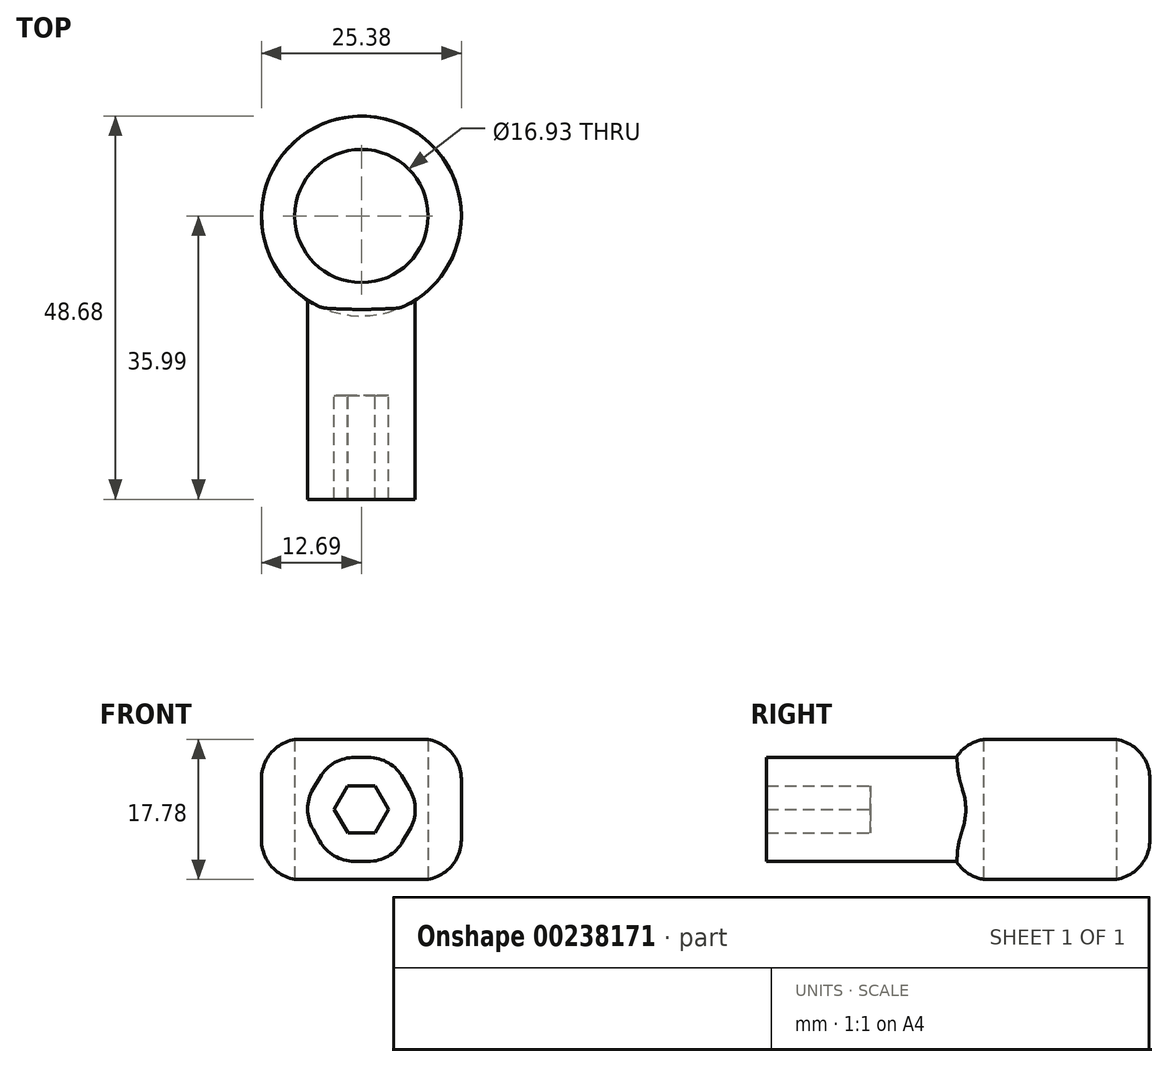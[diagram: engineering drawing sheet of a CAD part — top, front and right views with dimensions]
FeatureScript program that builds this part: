
annotation { "Feature Type Name" : "Feature", "Feature Type Description" : "" }
export const myFeature = defineFeature(function(context is Context, id is Id, definition is map)
    precondition{}
    {
        {
            var Q0;
            Q0=qCreatedBy(makeId("Front.planeOp"),FACE);
            var sketch = newSketch(context, id + "F0", { "sketchPlane" : qUnion([Q0])});
            skCircle(sketch, "E0.cCircle", {"center": v(0, 0) * mm, "radius": 3 * mm, "construction": true});
            skLineSegment(sketch, "E0.0", {"start": v(-1.72, -3) * mm, "end": v(-3.46, -0.01) * mm});
            skLineSegment(sketch, "E0.1", {"start": v(-3.46, -0.01) * mm, "end": v(-1.74, 3) * mm});
            skLineSegment(sketch, "E0.2", {"start": v(-1.74, 3) * mm, "end": v(1.72, 3) * mm});
            skLineSegment(sketch, "E0.3", {"start": v(1.72, 3) * mm, "end": v(3.46, 0.01) * mm});
            skLineSegment(sketch, "E0.4", {"start": v(3.46, 0.01) * mm, "end": v(1.74, -3) * mm});
            skLineSegment(sketch, "E0.5", {"start": v(1.74, -3) * mm, "end": v(-1.72, -3) * mm});
            skPoint(sketch, "E0.0.midPoint", {"position": v(-2.6, -1.51) * mm});
            skCircle(sketch, "E1.cCircle", {"center": v(0, 0) * mm, "radius": 6.6 * mm, "construction": true});
            skLineSegment(sketch, "E1.0", {"start": v(-7.62, 0.04) * mm, "end": v(-3.77, 6.62) * mm});
            skLineSegment(sketch, "E1.1", {"start": v(-3.77, 6.62) * mm, "end": v(3.85, 6.58) * mm});
            skLineSegment(sketch, "E1.2", {"start": v(3.85, 6.58) * mm, "end": v(7.62, -0.04) * mm});
            skLineSegment(sketch, "E1.3", {"start": v(7.62, -0.04) * mm, "end": v(3.77, -6.62) * mm});
            skLineSegment(sketch, "E1.4", {"start": v(3.77, -6.62) * mm, "end": v(-3.85, -6.58) * mm});
            skLineSegment(sketch, "E1.5", {"start": v(-3.85, -6.58) * mm, "end": v(-7.62, 0.04) * mm});
            skPoint(sketch, "E1.0.midPoint", {"position": v(-5.7, 3.33) * mm});
            skSolve(sketch);
        }
        {
            var Q0;
            Q0=makeQuery(id+"F0.imprint","IMPRINT",FACE,{"disambiguationData":[TD([[makeQuery(id+"F0.imprint","IMPRINT",EDGE,{"derivedFrom":sQuery(id+"F0.wireOp",EDGE,"E0.0")}),1.0]])]});
            extrude(context, id + "F1", {"entities" : qUnion([Q0]), "depth" : 25.4 * mm});
        }
        {
            var Q0;
            Q0=makeQuery(id+"F0.imprint","IMPRINT",FACE,{"disambiguationData":[TD([[makeQuery(id+"F0.imprint","IMPRINT",EDGE,{"derivedFrom":sQuery(id+"F0.wireOp",EDGE,"E0.0")}),-1.0]])]});
            extrude(context, id + "F2", {"entities" : qUnion([Q0]), "operationType" : NewBodyOperationType.ADD, "depth" : 12.2 * mm});
        }
        {
            var Q0;
            Q0=makeQuery(id+"F1.opExtrude","SWEPT_EDGE",EDGE,{"disambiguationData":[OSD([sQuery(id+"F0.wireOp",EDGE,"E1.3"),sQuery(id+"F0.wireOp",EDGE,"E1.4")])]});
            var Q1;
            Q1=makeQuery(id+"F1.opExtrude","SWEPT_EDGE",EDGE,{"disambiguationData":[OSD([sQuery(id+"F0.wireOp",EDGE,"E1.4"),sQuery(id+"F0.wireOp",EDGE,"E1.5")])]});
            var Q2;
            Q2=makeQuery(id+"F1.opExtrude","SWEPT_EDGE",EDGE,{"disambiguationData":[OSD([sQuery(id+"F0.wireOp",EDGE,"E1.0"),sQuery(id+"F0.wireOp",EDGE,"E1.5")])]});
            var Q3;
            Q3=makeQuery(id+"F1.opExtrude","SWEPT_EDGE",EDGE,{"disambiguationData":[OSD([sQuery(id+"F0.wireOp",EDGE,"E1.0"),sQuery(id+"F0.wireOp",EDGE,"E1.1")])]});
            var Q4;
            Q4=makeQuery(id+"F1.opExtrude","SWEPT_EDGE",EDGE,{"disambiguationData":[OSD([sQuery(id+"F0.wireOp",EDGE,"E1.1"),sQuery(id+"F0.wireOp",EDGE,"E1.2")])]});
            var Q5;
            Q5=makeQuery(id+"F1.opExtrude","SWEPT_EDGE",EDGE,{"disambiguationData":[OSD([sQuery(id+"F0.wireOp",EDGE,"E1.2"),sQuery(id+"F0.wireOp",EDGE,"E1.3")])]});
            fillet(context, id + "F3", {"entities" : qUnion([Q0, Q1, Q2, Q3, Q4, Q5]), "radius" : 5.08 * mm, "tangentPropagation" : true, "allowEdgeOverflow" : false});
        }
        {
            var Q0;
            Q0=qCreatedBy(makeId("Top.planeOp"),FACE);
            var sketch = newSketch(context, id + "F4", { "sketchPlane" : qUnion([Q0])});
            skPoint(sketch, "E2.first.point", {"position": v(0, 0) * mm});
            skPoint(sketch, "E2.second.point", {"position": v(0, 28.26) * mm});
            skPoint(sketch, "E2.third.point", {"position": v(-7.4, 26.23) * mm});
            skCircle(sketch, "E3", {"center": v(0, 10.6) * mm, "radius": 12.69 * mm});
            skCircle(sketch, "E4", {"center": v(0, 10.6) * mm, "radius": 8.46 * mm});
            skSolve(sketch);
        }
        {
            var Q0;
            Q0=makeQuery(id+"F4.imprint","IMPRINT",FACE,{"disambiguationData":[TD([[makeQuery(id+"F4.imprint","IMPRINT",EDGE,{"derivedFrom":sQuery(id+"F4.wireOp",EDGE,"E3")}),1.0]])]});
            extrude(context, id + "F5", {"entities" : qUnion([Q0]), "operationType" : NewBodyOperationType.ADD, "endBound" : BoundingType.SYMMETRIC, "depth" : 17.78 * mm});
        }
        {
            var Q0;
            Q0=makeQuery(id+"F5.opExtrude","CAP_EDGE",EDGE,{"disambiguationData":[OSD([sQuery(id+"F4.wireOp",EDGE,"E3")])],"isStart":true});
            var Q1;
            Q1=makeQuery(id+"F5.opExtrude","CAP_EDGE",EDGE,{"disambiguationData":[OSD([sQuery(id+"F4.wireOp",EDGE,"E3")])],"isStart":false});
            fillet(context, id + "F6", {"entities" : qUnion([Q0, Q1]), "radius" : 5.08 * mm, "tangentPropagation" : true, "allowEdgeOverflow" : false});
        }
    });
